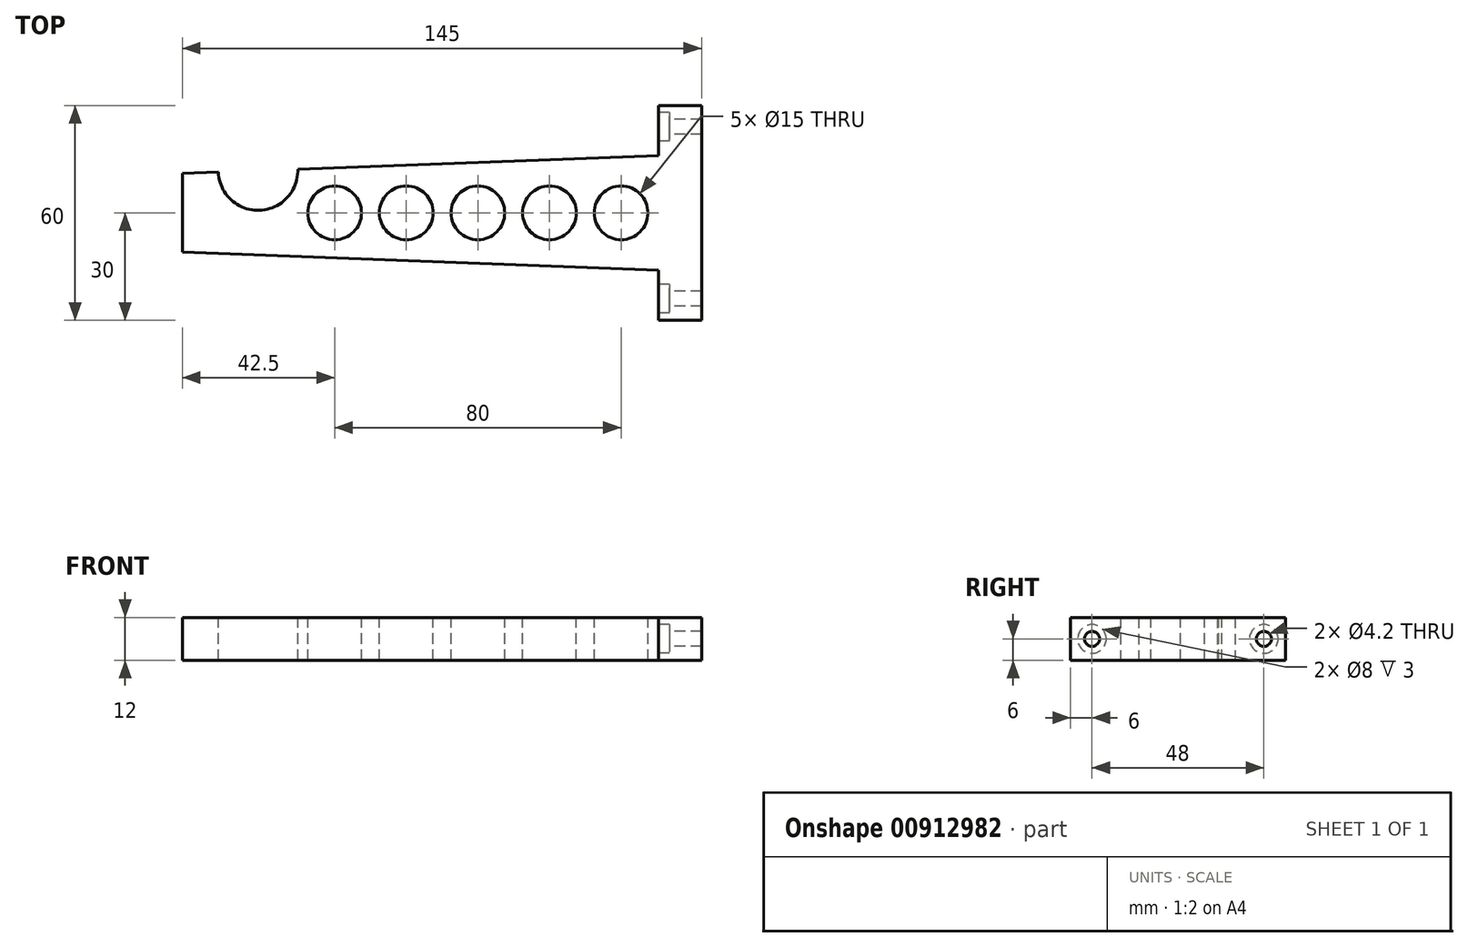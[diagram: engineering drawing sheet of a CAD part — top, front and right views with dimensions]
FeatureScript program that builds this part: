
annotation { "Feature Type Name" : "Feature", "Feature Type Description" : "" }
export const myFeature = defineFeature(function(context is Context, id is Id, definition is map)
    precondition{}
    {
        {
            var Q0;
            Q0=qCreatedBy(makeId("Top.planeOp"),FACE);
            var sketch = newSketch(context, id + "F0", { "sketchPlane" : qUnion([Q0])});
            skLineSegment(sketch, "E0.bottom", {"start": v(72.5, -30) * mm, "end": v(-72.5, -30) * mm});
            skLineSegment(sketch, "E0.top", {"start": v(72.5, 30) * mm, "end": v(-72.5, 30) * mm});
            skLineSegment(sketch, "E0.left", {"start": v(72.5, -30) * mm, "end": v(72.5, 30) * mm});
            skLineSegment(sketch, "E0.right", {"start": v(-72.5, -30) * mm, "end": v(-72.5, 30) * mm});
            skPoint(sketch, "E0.middle", {"position": v(0, 0) * mm});
            skPoint(sketch, "E1", {"position": v(-72.5, 11) * mm});
            skPoint(sketch, "E2", {"position": v(-72.5, -11) * mm});
            skPoint(sketch, "E3", {"position": v(-72.5, 0) * mm});
            skPoint(sketch, "E4", {"position": v(72.5, 0) * mm});
            skLineSegment(sketch, "E5", {"start": v(-72.5, 0) * mm, "end": v(72.5, 0) * mm, "construction": true});
            skPoint(sketch, "E6", {"position": v(60.5, 30) * mm});
            skPoint(sketch, "E7", {"position": v(60.5, -30) * mm});
            skLineSegment(sketch, "E8", {"start": v(60.5, 30) * mm, "end": v(60.5, -30) * mm});
            skPoint(sketch, "E9", {"position": v(60.5, 16) * mm});
            skPoint(sketch, "E10", {"position": v(60.5, -16) * mm});
            skLineSegment(sketch, "E11", {"start": v(-72.5, 11) * mm, "end": v(60.5, 16) * mm});
            skLineSegment(sketch, "E12", {"start": v(-72.5, -11) * mm, "end": v(60.5, -16) * mm});
            skSolve(sketch);
        }
        {
            var Q0;
            {var subQ4=sQuery(id+"F0.wireOp",EDGE,"E0.left");Q0=makeQuery(id+"F0.imprint","IMPRINT",FACE,{"disambiguationData":[TD([[makeQuery(id+"F0.imprint","IMPRINT",EDGE,{"derivedFrom":subQ4}),1.0]])]});}
            var Q1;
            {var subQ0=sQuery(id+"F0.wireOp",EDGE,"E11");Q1=makeQuery(id+"F0.imprint","IMPRINT",FACE,{"disambiguationData":[TD([[makeQuery(id+"F0.imprint","IMPRINT",EDGE,{"derivedFrom":subQ0}),-1.0]])]});}
            extrude(context, id + "F1", {"entities" : qUnion([Q0, Q1]), "depth" : 12 * mm, "offsetDistance" : 25 * mm});
        }
        {
            var Q0;
            Q0=makeQuery(id+"F1.opExtrude","CAP_FACE",FACE,{"disambiguationData":[OSD([sQuery(id+"F0.wireOp",EDGE,"E0.bottom"),sQuery(id+"F0.wireOp",EDGE,"E0.top"),sQuery(id+"F0.wireOp",EDGE,"E0.left"),sQuery(id+"F0.wireOp",EDGE,"E0.right"),sQuery(id+"F0.wireOp",EDGE,"E8"),sQuery(id+"F0.wireOp",EDGE,"E11"),sQuery(id+"F0.wireOp",EDGE,"E12")])],"isStart":false});
            var sketch = newSketch(context, id + "F2", { "sketchPlane" : qUnion([Q0])});
            skPoint(sketch, "E13", {"position": v(-51.4, -0.1) * mm});
            skPoint(sketch, "E14", {"position": v(-51.4, 11.8) * mm});
            skCircle(sketch, "E15", {"center": v(-51.4, 11.8) * mm, "radius": 11.1 * mm});
            skSolve(sketch);
        }
        {
            var Q0;
            Q0 = qSketchRegion(id + "F2", true);
            extrude(context, id + "F3", {"entities" : qUnion([Q0]), "operationType" : NewBodyOperationType.REMOVE, "endBound" : BoundingType.THROUGH_ALL, "oppositeDirection" : true, "depth" : 25 * mm, "offsetDistance" : 25 * mm});
        }
        {
            var Q0;
            Q0=qCreatedBy(makeId("Right.planeOp"),FACE);
            cPlane(context, id + "F4", {"entities" : qUnion([Q0]), "cplaneType" : CPlaneType.OFFSET, "offset" : 60.5 * mm, "width" : 150 * mm, "height" : 150 * mm});
        }
        {
            var Q0;
            Q0=qCreatedBy(id+"F4.planeOp",FACE);
            var sketch = newSketch(context, id + "F5", { "sketchPlane" : qUnion([Q0])});
            skPoint(sketch, "E16", {"position": v(24, 6) * mm});
            skPoint(sketch, "E17", {"position": v(-24, 6) * mm});
            skCircle(sketch, "E18", {"center": v(24, 6) * mm, "radius": 2.1 * mm});
            skCircle(sketch, "E19", {"center": v(-24, 6) * mm, "radius": 2.1 * mm});
            skSolve(sketch);
        }
        {
            var Q0;
            Q0 = qSketchRegion(id + "F5", true);
            extrude(context, id + "F6", {"entities" : qUnion([Q0]), "operationType" : NewBodyOperationType.REMOVE, "endBound" : BoundingType.THROUGH_ALL, "depth" : 25 * mm, "offsetDistance" : 25 * mm});
        }
        {
            var Q0;
            {var subQ0=sQuery(id+"F0.wireOp",EDGE,"E8");Q0=makeQuery(id+"F1.opExtrude","SWEPT_FACE",FACE,{"disambiguationData":[OSD([subQ0]),TDD([makeQuery(id+"F0.imprint","IMPRINT",EDGE,{"disambiguationData":[TD([[makeQuery(id+"F0.imprint","INTERSECT",VERTEX,{"derivedFrom":[sQuery(id+"F0.wireOp",EDGE,"E0.top"),subQ0]}),-1.0]])],"derivedFrom":subQ0})])]});}
            var sketch = newSketch(context, id + "F7", { "sketchPlane" : qUnion([Q0])});
            skPoint(sketch, "E20", {"position": v(-24, 6) * mm});
            skCircle(sketch, "E21", {"center": v(-24, 6) * mm, "radius": 4 * mm});
            skSolve(sketch);
        }
        {
            var Q0;
            Q0 = qSketchRegion(id + "F7", true);
            extrude(context, id + "F8", {"entities" : qUnion([Q0]), "operationType" : NewBodyOperationType.REMOVE, "oppositeDirection" : true, "depth" : 3 * mm, "offsetDistance" : 25 * mm});
        }
        {
            var Q0;
            {var subQ0=sQuery(id+"F0.wireOp",EDGE,"E8");Q0=makeQuery(id+"F1.opExtrude","SWEPT_FACE",FACE,{"disambiguationData":[OSD([subQ0]),TDD([makeQuery(id+"F0.imprint","IMPRINT",EDGE,{"disambiguationData":[TD([[makeQuery(id+"F0.imprint","INTERSECT",VERTEX,{"derivedFrom":[sQuery(id+"F0.wireOp",EDGE,"E0.bottom"),subQ0]}),1.0]])],"derivedFrom":subQ0})])]});}
            var sketch = newSketch(context, id + "F9", { "sketchPlane" : qUnion([Q0])});
            skPoint(sketch, "E22", {"position": v(24, 6) * mm});
            skCircle(sketch, "E23", {"center": v(24, 6) * mm, "radius": 4 * mm});
            skSolve(sketch);
        }
        {
            var Q0;
            Q0 = qSketchRegion(id + "F9", true);
            extrude(context, id + "F10", {"entities" : qUnion([Q0]), "operationType" : NewBodyOperationType.REMOVE, "oppositeDirection" : true, "depth" : 3 * mm, "offsetDistance" : 25 * mm});
        }
        {
            var Q0;
            Q0=makeQuery(id+"F1.opExtrude","CAP_FACE",FACE,{"disambiguationData":[OSD([sQuery(id+"F0.wireOp",EDGE,"E0.bottom"),sQuery(id+"F0.wireOp",EDGE,"E0.top"),sQuery(id+"F0.wireOp",EDGE,"E0.left"),sQuery(id+"F0.wireOp",EDGE,"E0.right"),sQuery(id+"F0.wireOp",EDGE,"E8"),sQuery(id+"F0.wireOp",EDGE,"E11"),sQuery(id+"F0.wireOp",EDGE,"E12")])],"isStart":false});
            var sketch = newSketch(context, id + "F11", { "sketchPlane" : qUnion([Q0])});
            skPoint(sketch, "E24", {"position": v(-30, 0) * mm});
            skPoint(sketch, "E25", {"position": v(-10, 0) * mm});
            skPoint(sketch, "E26", {"position": v(10, 0) * mm});
            skPoint(sketch, "E27", {"position": v(30, 0) * mm});
            skPoint(sketch, "E28", {"position": v(50, 0) * mm});
            skCircle(sketch, "E29", {"center": v(-30, 0) * mm, "radius": 7.5 * mm});
            skCircle(sketch, "E30", {"center": v(-10, 0) * mm, "radius": 7.5 * mm});
            skCircle(sketch, "E31", {"center": v(10, 0) * mm, "radius": 7.5 * mm});
            skCircle(sketch, "E32", {"center": v(30, 0) * mm, "radius": 7.5 * mm});
            skCircle(sketch, "E33", {"center": v(50, 0) * mm, "radius": 7.5 * mm});
            skSolve(sketch);
        }
        {
            var Q0;
            Q0 = qSketchRegion(id + "F11", true);
            extrude(context, id + "F12", {"entities" : qUnion([Q0]), "operationType" : NewBodyOperationType.REMOVE, "endBound" : BoundingType.THROUGH_ALL, "oppositeDirection" : true, "depth" : 25 * mm, "offsetDistance" : 25 * mm});
        }
    });
